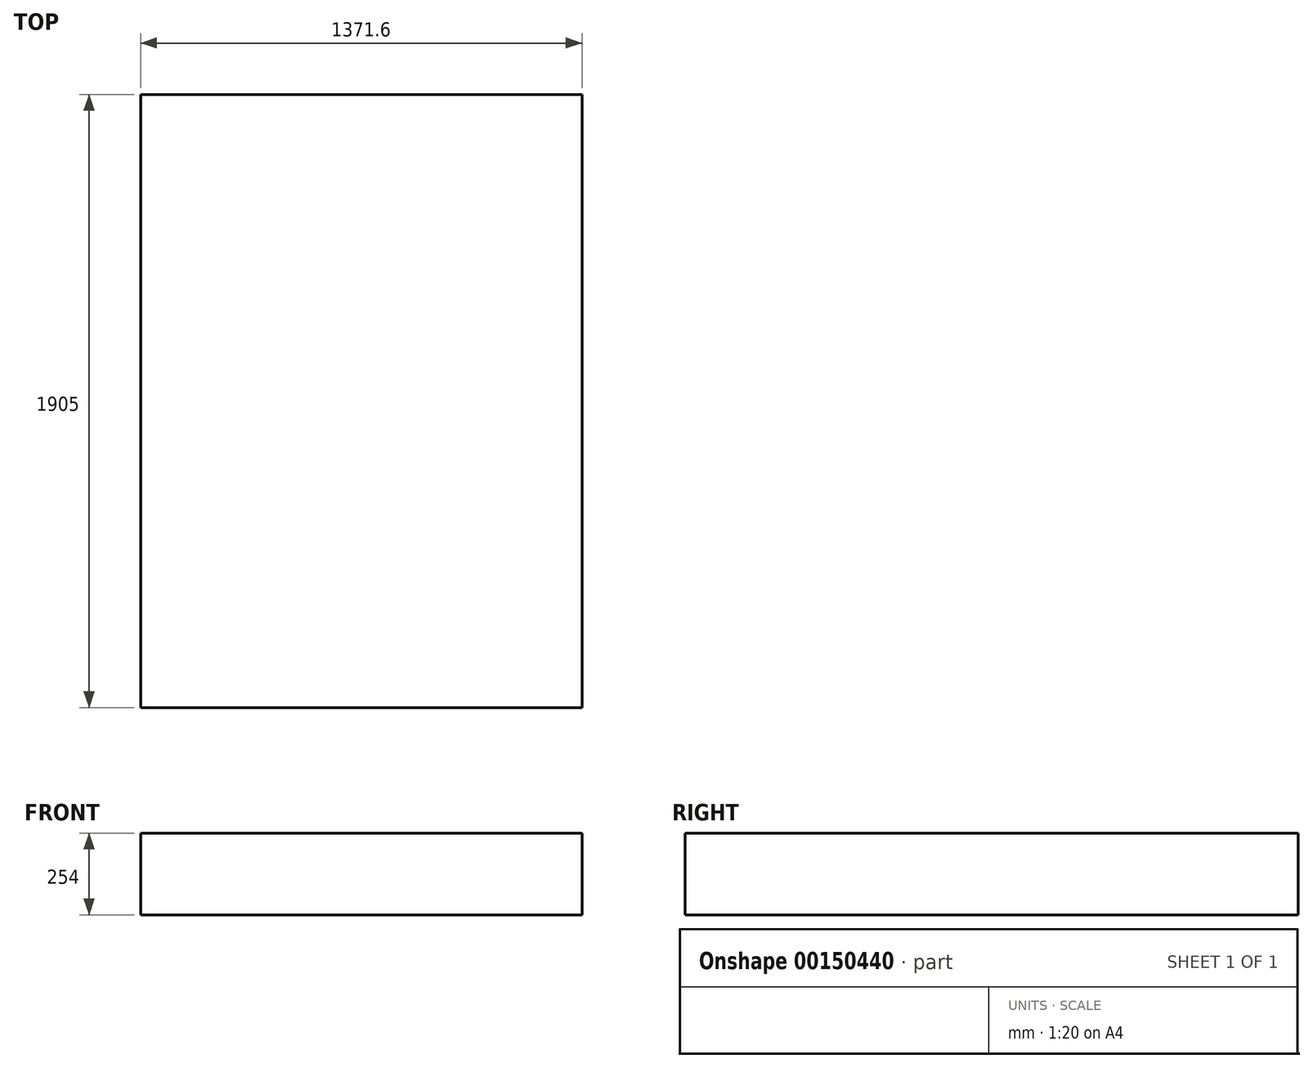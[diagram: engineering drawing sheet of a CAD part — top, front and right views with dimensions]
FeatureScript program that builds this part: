
annotation { "Feature Type Name" : "Feature", "Feature Type Description" : "" }
export const myFeature = defineFeature(function(context is Context, id is Id, definition is map)
    precondition{}
    {
        {
            var Q0;
            Q0=qCreatedBy(makeId("Top.planeOp"),FACE);
            var sketch = newSketch(context, id + "F0", { "sketchPlane" : qUnion([Q0])});
            skLineSegment(sketch, "E0.bottom", {"start": v(685.8, 952.5) * mm, "end": v(-685.8, 952.5) * mm});
            skLineSegment(sketch, "E0.top", {"start": v(685.8, -952.5) * mm, "end": v(-685.8, -952.5) * mm});
            skLineSegment(sketch, "E0.left", {"start": v(685.8, 952.5) * mm, "end": v(685.8, -952.5) * mm});
            skLineSegment(sketch, "E0.right", {"start": v(-685.8, 952.5) * mm, "end": v(-685.8, -952.5) * mm});
            skPoint(sketch, "E0.middle", {"position": v(0, 0) * mm});
            skSolve(sketch);
        }
        {
            var Q0;
            Q0 = qSketchRegion(id + "F0", true);
            extrude(context, id + "F1", {"entities" : qUnion([Q0]), "endBound" : BoundingType.SYMMETRIC, "depth" : 254 * mm});
        }
    });
